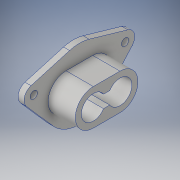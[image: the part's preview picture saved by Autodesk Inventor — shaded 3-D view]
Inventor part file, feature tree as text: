
AUTODESK INVENTOR PART (.ipt)
format: ipt  version: 2017 (Build 210142000, 142)  size: 177,664 bytes
history: native  units: in
note: dims shown in document units (in); Inventor stores cm internally (conversion verified against a paired STEP export)
features: extrude x2, sketch x1, projected_geometry x1
ambient origin geometry x8: Origin, YZ Plane, XZ Plane, XY Plane, X Axis, Y Axis, Z Axis, Center Point
bodies: Solid1 (feature_tree)
feature tree (4):
  extrude  "Extrusion6"  Depth=0.564in
  extrude  "Extrusion7"  Depth=0.564in
  sketch  "Sketch6"  dims[d5=1.4567in d6=0.8in d47=0.15in d48=0.15in d49=1.456in d50=0.276in d51=0.276in d52=0.945in d53=0.945in d54=0.4in d55=0.4in d56=0.495in d57=0.495in d58=0.5512in d59=90.0deg d60=90.0deg d61=0.728in d62=0.728in d63=0.2756in d64=0.2756in d71=0.26in d72=0.13in d73=0.125in d74=0.0in d75=0.2475in d76=0.2475in d77=0.745in d78=0.745in d79=0.564in d80=0.0in]
  projected_geometry  "Projected Loop5"
